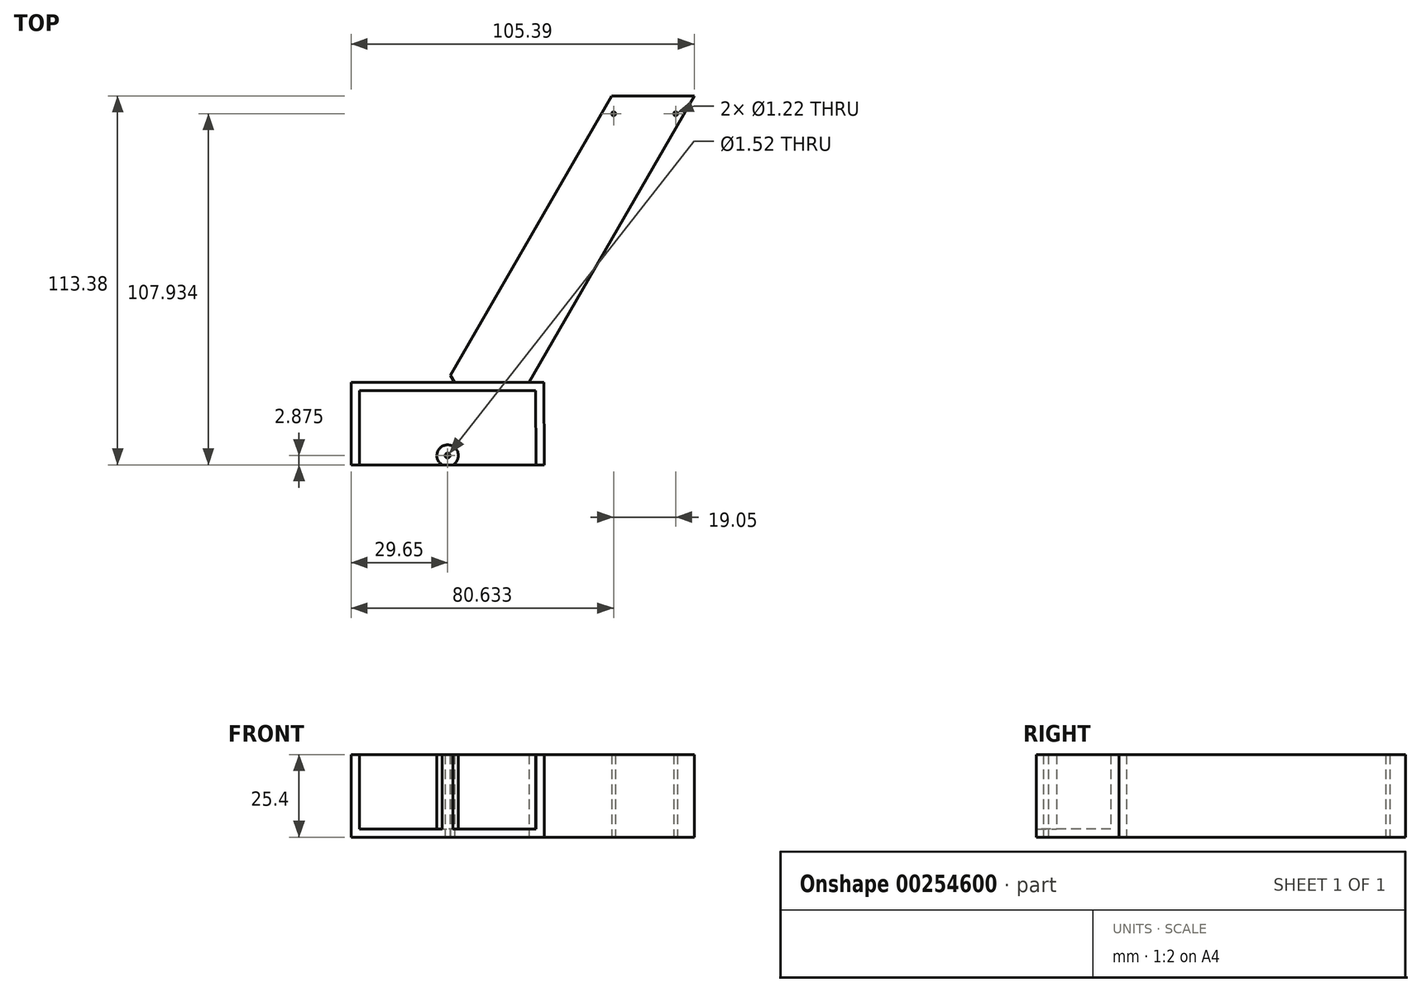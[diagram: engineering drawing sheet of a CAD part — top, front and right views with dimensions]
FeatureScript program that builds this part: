
annotation { "Feature Type Name" : "Feature", "Feature Type Description" : "" }
export const myFeature = defineFeature(function(context is Context, id is Id, definition is map)
    precondition{}
    {
        {
            var Q0;
            Q0=qCreatedBy(makeId("Top.planeOp"),FACE);
            var sketch = newSketch(context, id + "F0", { "sketchPlane" : qUnion([Q0])});
            skLineSegment(sketch, "E0.bottom", {"start": v(-29.65, -22.66) * mm, "end": v(29.55, -22.66) * mm});
            skLineSegment(sketch, "E0.top", {"start": v(-29.65, -48.06) * mm, "end": v(29.65, -48.06) * mm});
            skLineSegment(sketch, "E0.left", {"start": v(-29.65, -22.66) * mm, "end": v(-29.65, -48.06) * mm});
            skLineSegment(sketch, "E0.right", {"start": v(29.55, -22.66) * mm, "end": v(29.65, -48.06) * mm});
            skCircle(sketch, "E1", {"center": v(0, -45.19) * mm, "radius": 0.76 * mm});
            skLineSegment(sketch, "E2.bottom", {"start": v(-23.32, -22.66) * mm, "end": v(2.08, -22.66) * mm});
            skLineSegment(sketch, "E2.top", {"start": v(-74.12, 65.32) * mm, "end": v(-48.72, 65.32) * mm});
            skLineSegment(sketch, "E2.left", {"start": v(-23.32, -22.66) * mm, "end": v(-74.12, 65.32) * mm});
            skLineSegment(sketch, "E2.right", {"start": v(2.08, -22.66) * mm, "end": v(-48.72, 65.32) * mm});
            skLineSegment(sketch, "E3.bottom", {"start": v(-0.46, -22.66) * mm, "end": v(24.94, -22.66) * mm});
            skLineSegment(sketch, "E3.top", {"start": v(50.34, 65.32) * mm, "end": v(75.74, 65.32) * mm});
            skLineSegment(sketch, "E3.left", {"start": v(-0.46, -22.66) * mm, "end": v(50.34, 65.32) * mm});
            skLineSegment(sketch, "E3.right", {"start": v(24.94, -22.66) * mm, "end": v(75.74, 65.32) * mm});
            skCircle(sketch, "E4", {"center": v(-68.4, 59.87) * mm, "radius": 0.6 * mm});
            skCircle(sketch, "E5", {"center": v(-49.35, 59.87) * mm, "radius": 0.6 * mm});
            skCircle(sketch, "E6", {"center": v(50.98, 59.87) * mm, "radius": 0.6 * mm});
            skCircle(sketch, "E7", {"center": v(70.03, 59.87) * mm, "radius": 0.6 * mm});
            skLineSegment(sketch, "E8.bottom", {"start": v(-29.46, -48.06) * mm, "end": v(29.46, -48.06) * mm});
            skLineSegment(sketch, "E8.top", {"start": v(-29.46, -22.96) * mm, "end": v(29.46, -22.96) * mm});
            skLineSegment(sketch, "E8.left", {"start": v(-29.46, -48.06) * mm, "end": v(-29.46, -22.96) * mm});
            skLineSegment(sketch, "E8.right", {"start": v(29.46, -48.06) * mm, "end": v(29.46, -22.96) * mm});
            skSolve(sketch);
        }
        {
            var Q0;
            {var subQ4=sQuery(id+"F0.wireOp",EDGE,"E2.bottom");Q0=makeQuery(id+"F0.imprint","IMPRINT",FACE,{"disambiguationData":[TD([[makeQuery(id+"F0.imprint","IMPRINT",EDGE,{"derivedFrom":subQ4}),1.0]])]});}
            var Q1;
            {var subQ1=sQuery(id+"F0.wireOp",EDGE,"E3.top");Q1=makeQuery(id+"F0.imprint","IMPRINT",FACE,{"disambiguationData":[TD([[makeQuery(id+"F0.imprint","IMPRINT",EDGE,{"derivedFrom":subQ1}),-1.0]])]});}
            extrude(context, id + "F1", {"entities" : qUnion([Q0, Q1]), "depth" : 25.4 * mm});
        }
        {
            var Q0;
            Q0=makeQuery(id+"F0.imprint","IMPRINT",FACE,{"disambiguationData":[TD([[makeQuery(id+"F0.imprint","IMPRINT",EDGE,{"derivedFrom":sQuery(id+"F0.wireOp",EDGE,"E0.top")}),1.0]])]});
            extrude(context, id + "F2", {"entities" : qUnion([Q0]), "depth" : 25.4 * mm});
        }
        {
            var Q0;
            Q0=makeQuery(id+"F0.imprint","IMPRINT",FACE,{"disambiguationData":[TD([[makeQuery(id+"F0.imprint","IMPRINT",EDGE,{"derivedFrom":sQuery(id+"F0.wireOp",EDGE,"E1")}),-1.0]])]});
            extrude(context, id + "F3", {"entities" : qUnion([Q0]), "operationType" : NewBodyOperationType.ADD, "depth" : 25.4 * mm});
        }
        {
            var Q0;
            {var subQ0=sQuery(id+"F0.wireOp",EDGE,"E8.right");var subQ1=sQuery(id+"F0.wireOp",EDGE,"E8.left");var subQ2=sQuery(id+"F0.wireOp",EDGE,"E8.top");Q0=makeQuery(id+"F3.boolean.opBoolean","MERGE",FACE,{"derivedFrom":[makeQuery(id+"F2.opExtrude","CAP_FACE",FACE,{"disambiguationData":[OSD([sQuery(id+"F0.wireOp",EDGE,"E0.bottom"),sQuery(id+"F0.wireOp",EDGE,"E0.top"),sQuery(id+"F0.wireOp",EDGE,"E0.left"),sQuery(id+"F0.wireOp",EDGE,"E0.right"),sQuery(id+"F0.wireOp",EDGE,"E2.bottom"),sQuery(id+"F0.wireOp",EDGE,"E3.bottom"),subQ2,subQ1,subQ0])],"isStart":false}),makeQuery(id+"F3.opExtrude","CAP_FACE",FACE,{"disambiguationData":[OSD([sQuery(id+"F0.wireOp",EDGE,"E1"),sQuery(id+"F0.wireOp",EDGE,"E8.bottom"),subQ2,subQ1,subQ0])],"isStart":false})]});}
            var Q1;
            {var subQ0=sQuery(id+"F0.wireOp",EDGE,"E8.bottom");var subQ1=sQuery(id+"F0.wireOp",EDGE,"E0.top");Q1=makeQuery(id+"F3.boolean.opBoolean","MERGE",FACE,{"derivedFrom":[makeQuery(id+"F2.opExtrude","SWEPT_FACE",FACE,{"disambiguationData":[OSD([subQ1]),TDD([makeQuery(id+"F0.imprint","IMPRINT",EDGE,{"disambiguationData":[TD([[makeQuery(id+"F0.imprint","INTERSECT",VERTEX,{"derivedFrom":[subQ1,sQuery(id+"F0.wireOp",EDGE,"E0.left")]}),-1.0]])],"derivedFrom":subQ1})])]}),makeQuery(id+"F2.opExtrude","SWEPT_FACE",FACE,{"disambiguationData":[OSD([subQ1]),TDD([makeQuery(id+"F0.imprint","IMPRINT",EDGE,{"disambiguationData":[TD([[makeQuery(id+"F0.imprint","INTERSECT",VERTEX,{"derivedFrom":[subQ1,sQuery(id+"F0.wireOp",EDGE,"E0.right")]}),1.0]])],"derivedFrom":subQ1})])]}),makeQuery(id+"F3.opExtrude","SWEPT_FACE",FACE,{"disambiguationData":[OSD([subQ0])]})]});}
            shell(context, id + "F4", {"entities" : qUnion([Q0, Q1]), "thickness" : 2.54 * mm});
        }
    });
